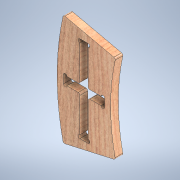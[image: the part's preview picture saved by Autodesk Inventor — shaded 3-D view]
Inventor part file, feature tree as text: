
AUTODESK INVENTOR PART (.ipt)
format: ipt  version: 2021 (Build 250183000, 183)  size: 166,400 bytes
history: native  units: mm
features: extrude x2, other x1, hole x1
ambient origin geometry x8: Origin, YZ Plane, XZ Plane, XY Plane, X Axis, Y Axis, Z Axis, Center Point
bodies: Solid1 (feature_tree)
feature tree (4):
  other  "CONTOURS"
  hole  "HOLES"  [1 undecoded]
  extrude  "Extrusion5"  Depth=18.0mm TaperAngle=0.0deg
  extrude  "Extrusion6"  [1 undecoded]
note: 2 required parameter values undecoded (feature->parameter linkage not recoverable at this tier; creation-order binding heuristic only, values carry confidence <= 0.55)
